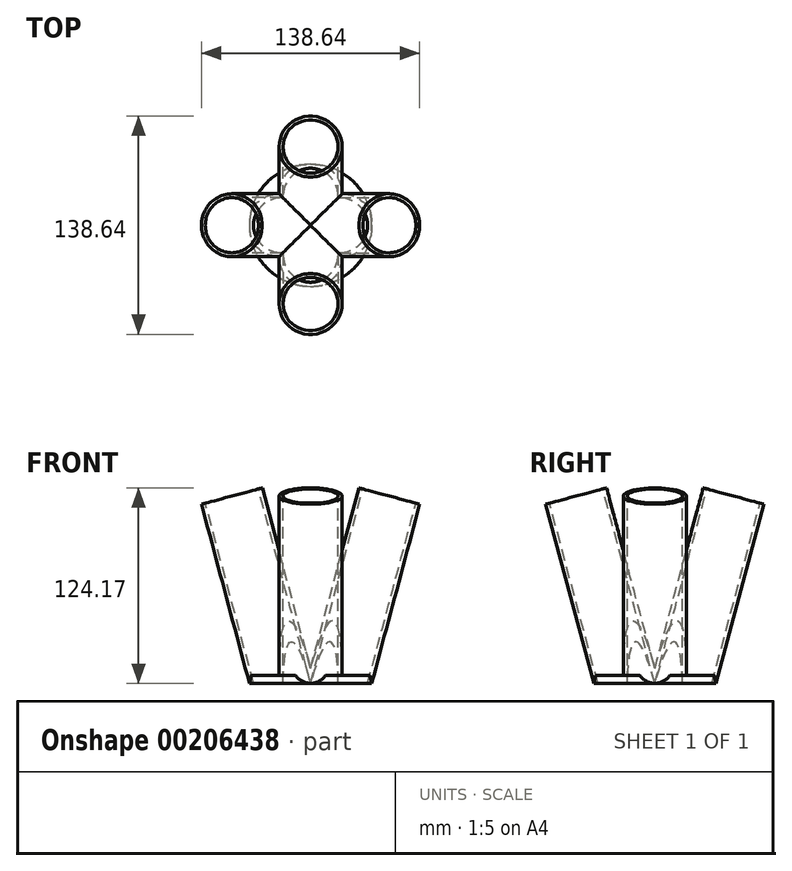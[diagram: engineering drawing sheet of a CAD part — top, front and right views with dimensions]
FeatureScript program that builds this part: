
annotation { "Feature Type Name" : "Feature", "Feature Type Description" : "" }
export const myFeature = defineFeature(function(context is Context, id is Id, definition is map)
    precondition{}
    {
        {
            var Q0;
            Q0=qCreatedBy(makeId("Top.planeOp"),FACE);
            var sketch = newSketch(context, id + "F0", { "sketchPlane" : qUnion([Q0])});
            skLineSegment(sketch, "E0", {"start": v(0, 50) * mm, "end": v(0, -50) * mm, "construction": true});
            skLineSegment(sketch, "E1", {"start": v(-50, 0) * mm, "end": v(50, 0) * mm, "construction": true});
            skPoint(sketch, "E2", {"position": v(0, 0) * mm});
            skLineSegment(sketch, "E3", {"start": v(-50, 15) * mm, "end": v(-50, -15) * mm});
            skPoint(sketch, "E4", {"position": v(-50, 0) * mm});
            skLineSegment(sketch, "E5", {"start": v(50, 15) * mm, "end": v(50, -15) * mm});
            skPoint(sketch, "E6", {"position": v(50, 0) * mm});
            skLineSegment(sketch, "E7", {"start": v(-15, -50) * mm, "end": v(15, -50) * mm});
            skLineSegment(sketch, "E8", {"start": v(-15, 50) * mm, "end": v(15, 50) * mm});
            skPoint(sketch, "E9", {"position": v(0, 50) * mm});
            skPoint(sketch, "E10", {"position": v(0, -50) * mm});
            skSolve(sketch);
        }
        {
            var Q0;
            Q0=sQuery(id+"F0.wireOp",EDGE,"E3");
            cPlane(context, id + "F1", {"entities" : qUnion([Q0]), "cplaneType" : CPlaneType.LINE_ANGLE, "offset" : 25 * mm, "angle" : 15 * degree, "width" : 150 * mm, "height" : 150 * mm});
        }
        {
            var Q0;
            Q0=sQuery(id+"F0.wireOp",EDGE,"E8");
            cPlane(context, id + "F2", {"entities" : qUnion([Q0]), "cplaneType" : CPlaneType.LINE_ANGLE, "offset" : 25 * mm, "angle" : 75 * degree, "width" : 150 * mm, "height" : 150 * mm});
        }
        {
            var Q0;
            Q0=sQuery(id+"F0.wireOp",EDGE,"E7");
            cPlane(context, id + "F3", {"entities" : qUnion([Q0]), "cplaneType" : CPlaneType.LINE_ANGLE, "offset" : 25 * mm, "angle" : 285 * degree, "width" : 150 * mm, "height" : 150 * mm});
        }
        {
            var Q0;
            Q0=sQuery(id+"F0.wireOp",EDGE,"E5");
            cPlane(context, id + "F4", {"entities" : qUnion([Q0]), "cplaneType" : CPlaneType.LINE_ANGLE, "offset" : 25 * mm, "angle" : 165 * degree, "width" : 150 * mm, "height" : 150 * mm});
        }
        {
            var Q0;
            Q0=qCreatedBy(id+"F1.planeOp",FACE);
            var sketch = newSketch(context, id + "F5", { "sketchPlane" : qUnion([Q0])});
            skPoint(sketch, "E11.0", {"position": v(-48.3, 0) * mm});
            skCircle(sketch, "E12", {"center": v(-48.3, 0) * mm, "radius": 17.5 * mm});
            skCircle(sketch, "E13.0", {"center": v(-48.3, 0) * mm, "radius": 20 * mm});
            skSolve(sketch);
        }
        {
            var Q0;
            Q0=makeQuery(id+"F5.imprint","IMPRINT",FACE,{"disambiguationData":[TD([[makeQuery(id+"F5.imprint","IMPRINT",EDGE,{"derivedFrom":sQuery(id+"F5.wireOp",EDGE,"E12")}),-1.0]])]});
            extrude(context, id + "F6", {"entities" : qUnion([Q0]), "depth" : 300 * mm});
        }
        {
            var Q0;
            Q0=qCreatedBy(id+"F3.planeOp",FACE);
            var sketch = newSketch(context, id + "F7", { "sketchPlane" : qUnion([Q0])});
            skPoint(sketch, "E14.0", {"position": v(0, 48.3) * mm});
            skCircle(sketch, "E15", {"center": v(0, 48.3) * mm, "radius": 17.5 * mm});
            skCircle(sketch, "E16.0", {"center": v(0, 48.3) * mm, "radius": 20 * mm});
            skSolve(sketch);
        }
        {
            var Q0;
            Q0 = qSketchRegion(id + "F7", true);
            extrude(context, id + "F8", {"entities" : qUnion([Q0]), "operationType" : NewBodyOperationType.ADD, "depth" : 300 * mm});
        }
        {
            var Q0;
            Q0=qCreatedBy(id+"F4.planeOp",FACE);
            var sketch = newSketch(context, id + "F9", { "sketchPlane" : qUnion([Q0])});
            skPoint(sketch, "E17.0", {"position": v(48.3, 0) * mm});
            skCircle(sketch, "E18", {"center": v(48.3, 0) * mm, "radius": 17.5 * mm});
            skCircle(sketch, "E19.0", {"center": v(48.3, 0) * mm, "radius": 20 * mm});
            skSolve(sketch);
        }
        {
            var Q0;
            Q0 = qSketchRegion(id + "F9", true);
            extrude(context, id + "F10", {"entities" : qUnion([Q0]), "operationType" : NewBodyOperationType.ADD, "oppositeDirection" : true, "depth" : 300 * mm});
        }
        {
            var Q0;
            Q0=qCreatedBy(id+"F2.planeOp",FACE);
            var sketch = newSketch(context, id + "F11", { "sketchPlane" : qUnion([Q0])});
            skPoint(sketch, "E20.0", {"position": v(0, 48.3) * mm});
            skCircle(sketch, "E21", {"center": v(0, 48.3) * mm, "radius": 17.5 * mm});
            skCircle(sketch, "E22.0", {"center": v(0, 48.3) * mm, "radius": 20 * mm});
            skSolve(sketch);
        }
        {
            var Q0;
            Q0 = qSketchRegion(id + "F11", true);
            extrude(context, id + "F12", {"entities" : qUnion([Q0]), "operationType" : NewBodyOperationType.ADD, "oppositeDirection" : true, "depth" : 300 * mm});
        }
        {
            var Q0;
            Q0=qCreatedBy(id+"F4.planeOp",FACE);
            var sketch = newSketch(context, id + "F13", { "sketchPlane" : qUnion([Q0])});
            skCircle(sketch, "E23.0", {"center": v(48.3, 0) * mm, "radius": 17.5 * mm});
            skSolve(sketch);
        }
        {
            var Q0;
            Q0 = qSketchRegion(id + "F13", true);
            extrude(context, id + "F14", {"entities" : qUnion([Q0]), "operationType" : NewBodyOperationType.REMOVE, "endBound" : BoundingType.THROUGH_ALL, "oppositeDirection" : true, "depth" : 25 * mm});
        }
        {
            var Q0;
            Q0=qCreatedBy(id+"F2.planeOp",FACE);
            var sketch = newSketch(context, id + "F15", { "sketchPlane" : qUnion([Q0])});
            skCircle(sketch, "E24.0", {"center": v(0, 48.3) * mm, "radius": 17.5 * mm});
            skSolve(sketch);
        }
        {
            var Q0;
            Q0 = qSketchRegion(id + "F15", true);
            extrude(context, id + "F16", {"entities" : qUnion([Q0]), "operationType" : NewBodyOperationType.REMOVE, "endBound" : BoundingType.THROUGH_ALL, "oppositeDirection" : true, "depth" : 25 * mm});
        }
        {
            var Q0;
            Q0=qCreatedBy(id+"F1.planeOp",FACE);
            var sketch = newSketch(context, id + "F17", { "sketchPlane" : qUnion([Q0])});
            skCircle(sketch, "E25.0", {"center": v(-48.3, 0) * mm, "radius": 17.5 * mm});
            skSolve(sketch);
        }
        {
            var Q0;
            Q0 = qSketchRegion(id + "F17", true);
            extrude(context, id + "F18", {"entities" : qUnion([Q0]), "operationType" : NewBodyOperationType.REMOVE, "endBound" : BoundingType.THROUGH_ALL, "depth" : 25 * mm});
        }
        {
            var Q0;
            Q0=qCreatedBy(id+"F3.planeOp",FACE);
            var sketch = newSketch(context, id + "F19", { "sketchPlane" : qUnion([Q0])});
            skCircle(sketch, "E26.0", {"center": v(0, 48.3) * mm, "radius": 17.5 * mm});
            skSolve(sketch);
        }
        {
            var Q0;
            Q0 = qSketchRegion(id + "F19", true);
            extrude(context, id + "F20", {"entities" : qUnion([Q0]), "operationType" : NewBodyOperationType.REMOVE, "endBound" : BoundingType.THROUGH_ALL, "depth" : 25 * mm});
        }
        {
            var Q0;
            Q0=qCreatedBy(makeId("Front.planeOp"),FACE);
            var sketch = newSketch(context, id + "F21", { "sketchPlane" : qUnion([Q0])});
            skLineSegment(sketch, "E27.bottom", {"start": v(-92.95, -186.6) * mm, "end": v(92.95, -186.6) * mm});
            skLineSegment(sketch, "E27.top", {"start": v(-92.95, -320.28) * mm, "end": v(92.95, -320.28) * mm});
            skLineSegment(sketch, "E27.left", {"start": v(-92.95, -186.6) * mm, "end": v(-92.95, -320.28) * mm});
            skLineSegment(sketch, "E27.right", {"start": v(92.95, -186.6) * mm, "end": v(92.95, -320.28) * mm});
            skPoint(sketch, "E28.0", {"position": v(0, -186.6) * mm});
            skSolve(sketch);
        }
        {
            var Q0;
            Q0 = qSketchRegion(id + "F21", true);
            extrude(context, id + "F22", {"entities" : qUnion([Q0]), "operationType" : NewBodyOperationType.REMOVE, "endBound" : BoundingType.SYMMETRIC, "oppositeDirection" : true, "depth" : 100 * mm});
        }
        {
            var Q0;
            {var subQ0=makeQuery(id+"F14.opExtrude","SWEPT_FACE",FACE,{"disambiguationData":[OSD([sQuery(id+"F13.wireOp",EDGE,"E23.0")])]});var subQ1=sQuery(id+"F11.wireOp",EDGE,"E21");var subQ2=makeQuery(id+"F12.opExtrude","SWEPT_FACE",FACE,{"disambiguationData":[OSD([subQ1])]});var subQ3=sQuery(id+"F9.wireOp",EDGE,"E19.0");var subQ4=sQuery(id+"F9.wireOp",EDGE,"E18");var subQ5=makeQuery(id+"F10.opExtrude","CAP_FACE",FACE,{"disambiguationData":[OSD([subQ4,subQ3])],"isStart":true});var subQ6=makeQuery(id+"F16.opExtrude","SWEPT_FACE",FACE,{"disambiguationData":[OSD([sQuery(id+"F15.wireOp",EDGE,"E24.0")])]});var subQ7=makeQuery(id+"F10.opExtrude","SWEPT_FACE",FACE,{"disambiguationData":[OSD([subQ4])]});var subQ8=makeQuery(id+"F6.opExtrude","SWEPT_FACE",FACE,{"disambiguationData":[OSD([sQuery(id+"F5.wireOp",EDGE,"E12")])]});var subQ9=makeQuery(id+"F8.opExtrude","SWEPT_FACE",FACE,{"disambiguationData":[OSD([sQuery(id+"F7.wireOp",EDGE,"E15")])]});var subQ10=makeQuery(id+"F10.boolean.opBoolean","SPLIT",FACE,{"disambiguationData":[TD([subQ8,subQ9,subQ7]),OD(3.0)],"derivedFrom":subQ7});var subQ11=sQuery(id+"F11.wireOp",EDGE,"E22.0");var subQ12=makeQuery(id+"F12.opExtrude","SWEPT_FACE",FACE,{"disambiguationData":[OSD([subQ11])]});var subQ13=makeQuery(id+"F10.boolean.opBoolean","SPLIT",FACE,{"disambiguationData":[TD([subQ8,subQ9,subQ7]),OD(0.0)],"derivedFrom":subQ7});var subQ14=makeQuery(id+"F8.opExtrude","SWEPT_FACE",FACE,{"disambiguationData":[OSD([sQuery(id+"F7.wireOp",EDGE,"E16.0")])]});var subQ15=makeQuery(id+"F10.opExtrude","CAP_FACE",FACE,{"disambiguationData":[OSD([subQ4,subQ3])],"isStart":false});var subQ16=makeQuery(id+"F6.opExtrude","SWEPT_FACE",FACE,{"disambiguationData":[OSD([sQuery(id+"F5.wireOp",EDGE,"E13.0")])]});var subQ17=makeQuery(id+"F10.boolean.opBoolean","SPLIT",FACE,{"disambiguationData":[TD([subQ16,subQ14,subQ15])],"derivedFrom":subQ7});var subQ18=makeQuery(id+"F10.boolean.opBoolean","SPLIT",FACE,{"disambiguationData":[TD([subQ16,subQ14,subQ5])],"derivedFrom":subQ7});var subQ19=makeQuery(id+"F10.opExtrude","SWEPT_FACE",FACE,{"disambiguationData":[OSD([subQ3])]});Q0=makeQuery(id+"F18.boolean.opBoolean","INTERSECT",VERTEX,{"disambiguationData":[OD(1.0)],"derivedFrom":[makeQuery(id+"F16.boolean.opBoolean","MERGE",FACE,{"derivedFrom":[makeQuery(id+"F12.boolean.opBoolean","SPLIT",FACE,{"disambiguationData":[TD([subQ16,subQ19,makeQuery(id+"F12.opExtrude","CAP_FACE",FACE,{"disambiguationData":[OSD([subQ1,subQ11])],"isStart":true})])],"derivedFrom":subQ2}),makeQuery(id+"F12.boolean.opBoolean","SPLIT",FACE,{"disambiguationData":[TD([subQ8,subQ14,subQ19]),OD(0.0)],"derivedFrom":subQ2}),makeQuery(id+"F12.boolean.opBoolean","SPLIT",FACE,{"disambiguationData":[TD([subQ9,subQ19]),OD(1.0)],"derivedFrom":subQ2}),subQ6]}),makeQuery(id+"F16.boolean.opBoolean","SPLIT",FACE,{"disambiguationData":[TD([subQ5])],"derivedFrom":makeQuery(id+"F14.boolean.opBoolean","MERGE",FACE,{"derivedFrom":[makeQuery(id+"F10.boolean.opBoolean","SPLIT",FACE,{"disambiguationData":[TD([subQ8,subQ14]),OD(0.0)],"derivedFrom":subQ7}),makeQuery(id+"F10.boolean.opBoolean","SPLIT",FACE,{"disambiguationData":[TD([subQ8,subQ14]),OD(1.0)],"derivedFrom":subQ7}),makeQuery(id+"F10.boolean.opBoolean","SPLIT",FACE,{"disambiguationData":[TD([subQ16,subQ9]),OD(0.0)],"derivedFrom":subQ7}),makeQuery(id+"F10.boolean.opBoolean","SPLIT",FACE,{"disambiguationData":[TD([subQ16,subQ9]),OD(1.0)],"derivedFrom":subQ7}),makeQuery(id+"F10.boolean.opBoolean","SPLIT",FACE,{"disambiguationData":[TD([subQ8,subQ9,subQ7]),OD(1.0)],"derivedFrom":subQ7}),makeQuery(id+"F10.boolean.opBoolean","SPLIT",FACE,{"disambiguationData":[TD([subQ8,subQ9,subQ7]),OD(2.0)],"derivedFrom":subQ7}),makeQuery(id+"F12.boolean.opBoolean","SPLIT",FACE,{"disambiguationData":[TD([subQ16])],"derivedFrom":subQ18}),makeQuery(id+"F12.boolean.opBoolean","SPLIT",FACE,{"disambiguationData":[TD([subQ12])],"derivedFrom":subQ18}),makeQuery(id+"F12.boolean.opBoolean","SPLIT",FACE,{"disambiguationData":[TD([subQ16])],"derivedFrom":subQ17}),makeQuery(id+"F12.boolean.opBoolean","SPLIT",FACE,{"disambiguationData":[TD([subQ12])],"derivedFrom":subQ17}),makeQuery(id+"F12.boolean.opBoolean","SPLIT",FACE,{"disambiguationData":[TD([subQ8,subQ12])],"derivedFrom":subQ13}),makeQuery(id+"F12.boolean.opBoolean","SPLIT",FACE,{"disambiguationData":[TD([subQ8,subQ9,subQ7,subQ2]),OD(0.0)],"derivedFrom":subQ13}),makeQuery(id+"F12.boolean.opBoolean","SPLIT",FACE,{"disambiguationData":[TD([subQ8,subQ9,subQ7,subQ2]),OD(1.0)],"derivedFrom":subQ13}),makeQuery(id+"F12.boolean.opBoolean","SPLIT",FACE,{"disambiguationData":[TD([subQ8,subQ12])],"derivedFrom":subQ10}),makeQuery(id+"F12.boolean.opBoolean","SPLIT",FACE,{"disambiguationData":[TD([subQ8,subQ9,subQ7,subQ2]),OD(0.0)],"derivedFrom":subQ10}),makeQuery(id+"F12.boolean.opBoolean","SPLIT",FACE,{"disambiguationData":[TD([subQ8,subQ9,subQ7,subQ2]),OD(1.0)],"derivedFrom":subQ10}),subQ0]})}),makeQuery(id+"F18.opExtrude","SWEPT_FACE",FACE,{"disambiguationData":[OSD([sQuery(id+"F17.wireOp",EDGE,"E25.0")])]})]});}
            var Q1;
            Q1=qCreatedBy(makeId("Top.planeOp"),FACE);
            cPlane(context, id + "F23", {"entities" : qUnion([Q0, Q1]), "cplaneType" : CPlaneType.PLANE_POINT, "offset" : 25 * mm, "width" : 150 * mm, "height" : 150 * mm});
        }
        {
            var Q0;
            Q0=qCreatedBy(id+"F23.planeOp",FACE);
            var sketch = newSketch(context, id + "F24", { "sketchPlane" : qUnion([Q0])});
            skPoint(sketch, "E29.0", {"position": v(0, 0) * mm});
            skLineSegment(sketch, "E30.bottom", {"start": v(-50.92, 53.72) * mm, "end": v(50.92, 53.72) * mm});
            skLineSegment(sketch, "E30.top", {"start": v(-50.92, -53.72) * mm, "end": v(50.92, -53.72) * mm});
            skLineSegment(sketch, "E30.left", {"start": v(-50.92, 53.72) * mm, "end": v(-50.92, -53.72) * mm});
            skLineSegment(sketch, "E30.right", {"start": v(50.92, 53.72) * mm, "end": v(50.92, -53.72) * mm});
            skSolve(sketch);
        }
        {
            var Q0;
            Q0 = qSketchRegion(id + "F24", true);
            extrude(context, id + "F25", {"entities" : qUnion([Q0]), "operationType" : NewBodyOperationType.REMOVE, "endBound" : BoundingType.THROUGH_ALL, "oppositeDirection" : true, "depth" : 25 * mm});
        }
        {
            var Q0;
            Q0=makeQuery(id+"F25.boolean.opBoolean","COPY",FACE,{"derivedFrom":makeQuery(id+"F25.opExtrude","CAP_FACE",FACE,{"disambiguationData":[OSD([sQuery(id+"F24.wireOp",EDGE,"E30.bottom"),sQuery(id+"F24.wireOp",EDGE,"E30.top"),sQuery(id+"F24.wireOp",EDGE,"E30.left"),sQuery(id+"F24.wireOp",EDGE,"E30.right")])],"isStart":true})});
            var sketch = newSketch(context, id + "F26", { "sketchPlane" : qUnion([Q0])});
            skCircle(sketch, "E31", {"center": v(0, 0) * mm, "radius": 38.82 * mm});
            skEllipticalArc(sketch, "E32.0", {});
            skEllipticalArc(sketch, "E33.0", {});
            skEllipticalArc(sketch, "E34.0", {});
            skEllipticalArc(sketch, "E35.0", {});
            const initialGuessF26  = {"E32.0": [0, 0.018117333157176535, 0, 1, 0.02070552360820166, 0.02, 4.799742857365066, 1.4834424498145202], "E33.0": [-0.018117333157176486, 0, -1, 0, 0.02070552360820166, 0.02, 4.799742857365066, 1.4834424498145202], "E34.0": [0, -0.018117333157176486, 0, -1, 0.02070552360820166, 0.02, 4.799742857365068, 1.4834424498145182], "E35.0": [0.018117333157176438, 0, 1, 0, 0.020705523608201663, 0.02, 4.799742857365069, 1.48344244981452]};
            skSetInitialGuess(sketch, initialGuessF26);
            skSolve(sketch);
        }
        {
            var Q0;
            {var subQ0=sQuery(id+"F26.wireOp",EDGE,"E32.0");var subQ1=sQuery(id+"F26.wireOp",EDGE,"E31");var subQ2=makeQuery(id+"F26.imprint","INTERSECT",VERTEX,{"derivedFrom":[subQ1,subQ0]});Q0=makeQuery(id+"F26.imprint","IMPRINT",FACE,{"disambiguationData":[TD([[makeQuery(id+"F26.imprint","IMPRINT",EDGE,{"disambiguationData":[TD([[subQ2,-1.0]])],"derivedFrom":subQ1}),1.0]])]});}
            var Q1;
            {var subQ0=sQuery(id+"F26.wireOp",EDGE,"E33.0");var subQ1=sQuery(id+"F26.wireOp",EDGE,"E31");var subQ2=makeQuery(id+"F26.imprint","INTERSECT",VERTEX,{"derivedFrom":[subQ1,subQ0]});Q1=makeQuery(id+"F26.imprint","IMPRINT",FACE,{"disambiguationData":[TD([[makeQuery(id+"F26.imprint","IMPRINT",EDGE,{"disambiguationData":[TD([[subQ2,-1.0]])],"derivedFrom":subQ1}),1.0]])]});}
            var Q2;
            {var subQ0=sQuery(id+"F26.wireOp",EDGE,"E34.0");var subQ1=sQuery(id+"F26.wireOp",EDGE,"E31");var subQ2=makeQuery(id+"F26.imprint","INTERSECT",VERTEX,{"derivedFrom":[subQ1,subQ0]});Q2=makeQuery(id+"F26.imprint","IMPRINT",FACE,{"disambiguationData":[TD([[makeQuery(id+"F26.imprint","IMPRINT",EDGE,{"disambiguationData":[TD([[subQ2,-1.0]])],"derivedFrom":subQ1}),1.0]])]});}
            var Q3;
            {var subQ0=sQuery(id+"F26.wireOp",EDGE,"E32.0");var subQ1=sQuery(id+"F26.wireOp",EDGE,"E31");var subQ2=makeQuery(id+"F26.imprint","INTERSECT",VERTEX,{"derivedFrom":[subQ1,subQ0]});Q3=makeQuery(id+"F26.imprint","IMPRINT",FACE,{"disambiguationData":[TD([[makeQuery(id+"F26.imprint","IMPRINT",EDGE,{"disambiguationData":[TD([[subQ2,1.0]])],"derivedFrom":subQ1}),1.0]])]});}
            extrude(context, id + "F27", {"entities" : qUnion([Q0, Q1, Q2, Q3]), "operationType" : NewBodyOperationType.ADD, "oppositeDirection" : true, "depth" : 5 * mm});
        }
    });
